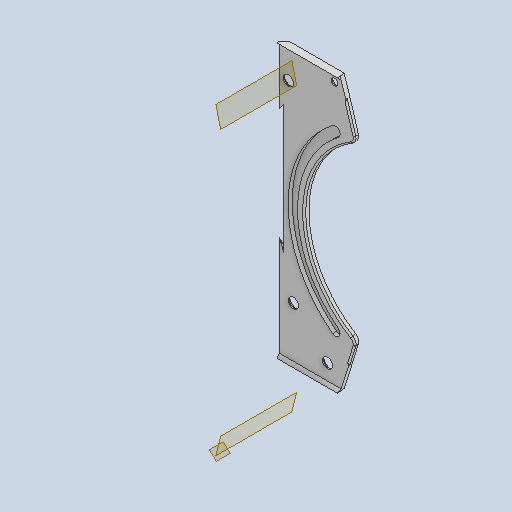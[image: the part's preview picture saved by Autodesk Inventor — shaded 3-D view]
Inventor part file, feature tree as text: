
AUTODESK INVENTOR PART (.ipt)
format: ipt  version: 2022 (Build 260153000, 153)  size: 2,899,456 bytes
history: native  units: mm
features: reference x95, projected_geometry x41, sketch x32, extrude x32, other x31, fillet x20, mirror x12, chamfer x6, revolve x3
ambient origin geometry x8: Origin, YZ Plane, XZ Plane, XY Plane, X Axis, Y Axis, Z Axis, Center Point
bodies: Body1 (feature_tree)
feature tree (272):
  other  "Твердое тело1"
  sketch  "Эскиз1"
  extrude  "Выдавливание1"  Depth=3.490659mm
  extrude  "Выдавливание2"  Depth=3.490659mm
  extrude  "Выдавливание3"  Depth=1.0mm
  sketch  "Эскиз5"
  extrude  "Выдавливание4"  Depth=1.0mm
  extrude  "Выдавливание5"  Depth=4.537856mm
  other  "РабПлоскость1"
  extrude  "Выдавливание6"  Depth=4.537856mm
  extrude  "Выдавливание7"  Depth=0.5mm
  extrude  "Выдавливание8"  Depth=18.69mm TaperAngle=0.0deg
  fillet  "Сопряжение2"  Radius=20.45mm
  extrude  "Выдавливание9"  Depth=1.5mm TaperAngle=0.0deg
  extrude  "Выдавливание10"  Depth=1.5mm
  fillet  "Сопряжение3"  Radius=3.0mm
  fillet  "Сопряжение4"  [1 undecoded]
  extrude  "Выдавливание11"  Depth=9.162979mm
  fillet  "Сопряжение6"  Radius=2.0mm
  fillet  "Сопряжение7"  Radius=28.843311mm
  extrude  "Выдавливание12"  Depth=1.5mm
  extrude  "Выдавливание13"  Depth=1.2mm
  fillet  "Сопряжение8"  Radius=20.69mm
  revolve  "Вращение1"
  fillet  "Сопряжение9"  Radius=11.0mm
  fillet  "Сопряжение10"  Radius=1.3mm
  extrude  "Выдавливание14"  Depth=14.5mm
  fillet  "Сопряжение11"  Radius=11.0mm
  fillet  "Сопряжение12"  Radius=9.0mm
  fillet  "Сопряжение13"  Radius=9.0mm
  chamfer  "Фаска1"  Distance=2.0mm
  extrude  "Выдавливание15"  Depth=1.0mm
  fillet  "Сопряжение14"  Radius=0.3mm
  extrude  "Выдавливание16"  Depth=0.3mm
  extrude  "Выдавливание17"  Depth=0.3mm
  revolve  "Вращение2"
  extrude  "Выдавливание18"  Depth=0.3mm
  mirror  "Зеркальное отражение2"
  other  "РабПлоскость4"
  extrude  "Выдавливание19"  Depth=25.0mm TaperAngle=0.0deg
  mirror  "Зеркальное отражение3"
  mirror  "Зеркальное отражение4"
  fillet  "Сопряжение18"  Radius=0.3mm
  extrude  "Выдавливание21"  Depth=2.0mm TaperAngle=0.0deg
  mirror  "Зеркальное отражение5"
  extrude  "Выдавливание22"  Depth=10.0mm TaperAngle=0.0deg
  mirror  "Зеркальное отражение6"
  extrude  "Выдавливание23"  Depth=1.0mm
  other  "РабПлоскость2"
  extrude  "Выдавливание24"  Depth=0.7mm
  extrude  "Выдавливание25"  Depth=0.7mm
  fillet  "Сопряжение20"  Radius=0.3mm
  fillet  "Сопряжение21"  Radius=0.2mm
  mirror  "Зеркальное отражение7"
  extrude  "Выдавливание26"  Depth=0.2mm TaperAngle=0.0deg
  mirror  "Зеркальное отражение8"
  mirror  "Зеркальное отражение9"
  revolve  "Вращение4"
  fillet  "Сопряжение26"  Radius=0.5mm
  fillet  "Сопряжение27"  Radius=3.5mm
  extrude  "Выдавливание27"  Depth=0.8mm
  mirror  "Зеркальное отражение10"
  extrude  "Выдавливание28"  Depth=2.0mm
  chamfer  "Фаска3"  Distance=2.0mm
  fillet  "Сопряжение28"  Radius=200.0mm
  extrude  "Выдавливание29"  Depth=0.5mm
  chamfer  "Фаска4"  Distance=0.5mm
  fillet  "Сопряжение29"  Radius=2.0mm
  mirror  "Зеркальное отражение11"
  mirror  "Зеркальное отражение12"
  extrude  "Выдавливание30"  Depth=2.0mm TaperAngle=0.0deg
  mirror  "Зеркальное отражение13"
  fillet  "Сопряжение30"  Radius=0.5mm
  chamfer  "Фаска5"  Distance=3.490659mm
  extrude  "Выдавливание31"  Depth=2.0mm
  extrude  "Выдавливание32"  TaperAngle=360.0deg  [1 undecoded]
  chamfer  "Фаска6"  Distance=0.7mm
  extrude  "Выдавливание33"  Depth=2.0mm
  chamfer  "Фаска7"  Distance=0.8mm
  reference  "Ссылка1"
  reference  "Ссылка2"
  reference  "Ссылка3"
  reference  "Ссылка4"
  reference  "Ссылка5"
  reference  "Ссылка6"
  reference  "Ссылка7"
  reference  "Ссылка8"
  reference  "Ссылка9"
  reference  "Ссылка10"
  reference  "Ссылка11"
  reference  "Ссылка12"
  reference  "Ссылка13"
  reference  "Ссылка14"
  reference  "Ссылка15"
  reference  "Ссылка16"
  reference  "Ссылка17"
  reference  "Ссылка18"
  reference  "Ссылка19"
  reference  "Ссылка20"
  reference  "Ссылка21"
  reference  "Ссылка22"
  reference  "Ссылка23"
  reference  "Ссылка24"
  reference  "Ссылка25"
  sketch  "Эскиз2"
  reference  "Ссылка26"
  reference  "Ссылка27"
  reference  "Ссылка28"
  reference  "Ссылка29"
  reference  "Ссылка30"
  sketch  "Эскиз3"
  projected_geometry  "Спроецированная петля1"
  projected_geometry  "Спроецированная петля2"
  reference  "Ссылка31"
  sketch  "Эскиз4"
  projected_geometry  "Спроецированная петля3"
  reference  "Ссылка32"
  projected_geometry  "Спроецированная петля4"
  projected_geometry  "Спроецированная петля5"
  reference  "Ссылка33"
  reference  "Ссылка34"
  reference  "Ссылка35"
  reference  "Ссылка47"
  sketch  "Эскиз6"
  projected_geometry  "Спроецированная петля6"
  sketch  "Эскиз7"
  projected_geometry  "Спроецированная петля7"
  sketch  "Эскиз8"
  reference  "Ссылка51"
  projected_geometry  "Спроецированная петля8"
  sketch  "Эскиз10"
  reference  "Ссылка54"
  reference  "Ссылка55"
  reference  "Ссылка56"
  reference  "Ссылка57"
  reference  "Ссылка58"
  sketch  "Эскиз11"
  projected_geometry  "Спроецированная петля9"
  sketch  "Эскиз12"
  projected_geometry  "Спроецированная петля10"
  reference  "Ссылка59"
  reference  "Ссылка60"
  reference  "Ссылка61"
  sketch  "Эскиз13"
  reference  "Ссылка62"
  reference  "Ссылка63"
  reference  "Ссылка64"
  reference  "Ссылка65"
  sketch  "Эскиз14"
  reference  "Ссылка66"
  projected_geometry  "Спроецированная петля11"
  sketch  "Эскиз15"
  projected_geometry  "Спроецированная петля12"
  sketch  "Эскиз16"
  reference  "Ссылка67"
  reference  "Ссылка68"
  reference  "Ссылка69"
  reference  "Ссылка70"
  reference  "Ссылка71"
  reference  "Ссылка72"
  sketch  "Эскиз17"
  reference  "Ссылка73"
  reference  "Ссылка74"
  projected_geometry  "Спроецированная петля13"
  projected_geometry  "Спроецированная петля14"
  reference  "Ссылка75"
  reference  "Ссылка76"
  sketch  "Эскиз18"
  reference  "Ссылка77"
  reference  "Ссылка78"
  reference  "Ссылка79"
  reference  "Ссылка80"
  reference  "Ссылка81"
  reference  "Ссылка82"
  reference  "Ссылка83"
  reference  "Ссылка84"
  sketch  "Эскиз19"
  projected_geometry  "Спроецированная петля15"
  projected_geometry  "Спроецированная петля16"
  projected_geometry  "Спроецированная петля17"
  sketch  "Эскиз20"
  sketch  "Эскиз21"
  sketch  "Эскиз22"
  projected_geometry  "Спроецированная петля19"
  projected_geometry  "Спроецированная петля23"
  reference  "Ссылка95"
  reference  "Ссылка96"
  reference  "Ссылка97"
  projected_geometry  "Спроецированная петля24"
  projected_geometry  "Спроецированная петля25"
  projected_geometry  "Спроецированная петля26"
  projected_geometry  "Спроецированная петля27"
  projected_geometry  "Спроецированная петля28"
  projected_geometry  "Спроецированная петля29"
  projected_geometry  "Спроецированная петля30"
  reference  "Ссылка103"
  reference  "Ссылка104"
  reference  "Ссылка105"
  reference  "Ссылка106"
  sketch  "Эскиз27"
  reference  "Ссылка107"
  projected_geometry  "Спроецированная петля31"
  projected_geometry  "Спроецированная петля32"
  reference  "Ссылка108"
  reference  "Ссылка109"
  reference  "Ссылка110"
  sketch  "Эскиз28"
  reference  "Ссылка111"
  projected_geometry  "Спроецированная петля33"
  sketch  "Эскиз29"
  reference  "Ссылка112"
  sketch  "Эскиз30"
  projected_geometry  "Спроецированная петля34"
  other  "РабПлоскость3"
  reference  "Ссылка113"
  projected_geometry  "Спроецированная петля35"
  sketch  "Эскиз32"
  projected_geometry  "Спроецированная петля37"
  projected_geometry  "Спроецированная петля38"
  sketch  "Эскиз33"
  sketch  "Эскиз34"
  projected_geometry  "Спроецированная петля39"
  projected_geometry  "Спроецированная петля40"
  projected_geometry  "Спроецированная петля41"
  projected_geometry  "Спроецированная петля42"
  projected_geometry  "Спроецированная петля43"
  sketch  "Эскиз36"
  projected_geometry  "Спроецированная петля44"
  reference  "Ссылка114"
  reference  "Ссылка115"
  reference  "Ссылка116"
  sketch  "Эскиз37"
  projected_geometry  "Спроецированная петля45"
  reference  "Ссылка117"
  reference  "Ссылка118"
  reference  "Ссылка119"
  reference  "Ссылка120"
  reference  "Ссылка121"
  reference  "Ссылка122"
  sketch  "Эскиз38"
  reference  "Ссылка123"
  reference  "Ссылка124"
  reference  "Ссылка125"
  reference  "Ссылка126"
  sketch  "Эскиз40"
  projected_geometry  "Спроецированная петля46"
  other  "<userpath>\Documents\Git\MZCAT_2024\MZCAT_2.iam"
  other  "MZCAT_2.iam"
  other  "lidar_krestovina:1"
  other  "shatun_lidar:1"
  other  "stabilisator_plan:1"
  other  "OCS-D008 B:3"
  other  "commutationCATboard:1"
  other  "CAT_protector:1"
  other  "OCS-D008 B:2"
  other  "<userpath>\Documents\Git\MZCAT_2024\MZCAT_4.iam"
  other  "MZCAT_4.iam"
  other  "vydacha_pusher:2"
  other  "FastBattery:1"
  other  "metal_cap:1"
  other  "base plate:1"
  other  "base plate:2"
  other  "<userpath>\Documents\Git\MZCAT_2024\MZCAT_3.iam"
  other  "MZCAT_3.iam"
  other  "akkum_cup:1"
  other  "vydacha_slide:1"
  other  "ov13855:1"
  other  "shelka_lidar:1"
  other  "shelka_lidar:2"
  other  "ov13855:2"
  other  "lidar_krestovina_base:1"
  other  "<userpath>\Documents\Git\MZCAT_2024\MZCAT_4.iam"
note: 2 required parameter values undecoded (feature->parameter linkage not recoverable at this tier; creation-order binding heuristic only, values carry confidence <= 0.55)
